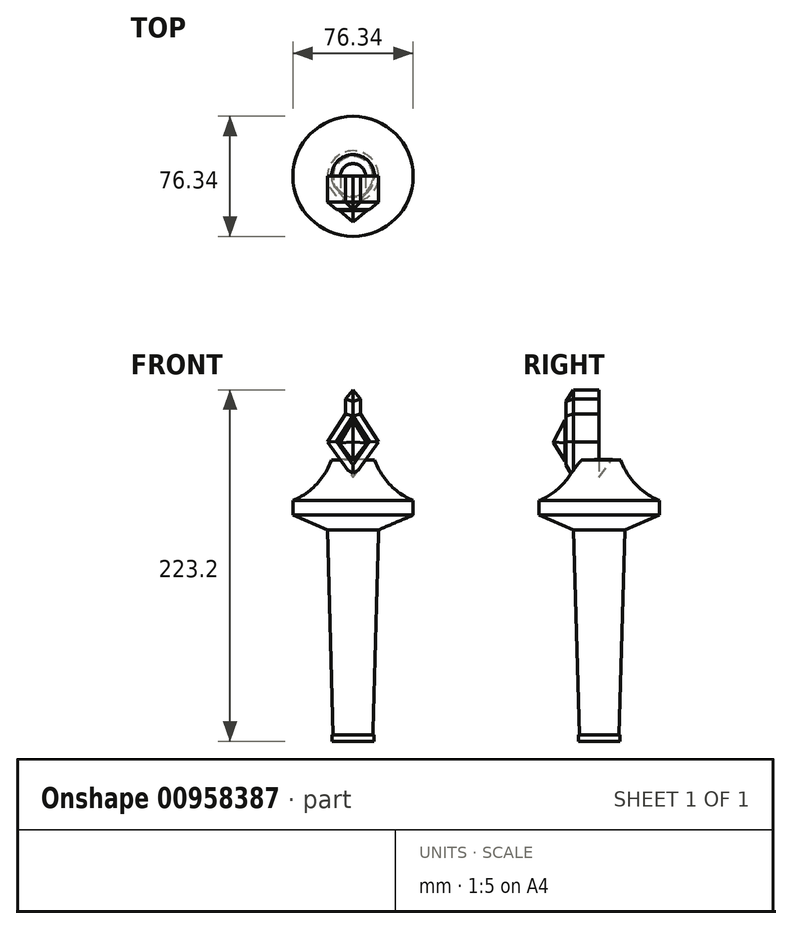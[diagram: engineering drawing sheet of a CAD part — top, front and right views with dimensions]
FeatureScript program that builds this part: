
annotation { "Feature Type Name" : "Feature", "Feature Type Description" : "" }
export const myFeature = defineFeature(function(context is Context, id is Id, definition is map)
    precondition{}
    {
        {
            var Q0;
            Q0=qCreatedBy(makeId("Front.planeOp"),FACE);
            var sketch = newSketch(context, id + "F0", { "sketchPlane" : qUnion([Q0])});
            skPoint(sketch, "E0", {"position": v(0, 703.66) * mm});
            skPoint(sketch, "E1", {"position": v(-33.04, 561.22) * mm});
            skPoint(sketch, "E2", {"position": v(33.12, 559.68) * mm});
            skPoint(sketch, "E3", {"position": v(0, 643.14) * mm});
            skPoint(sketch, "E4", {"position": v(-21.24, 561.22) * mm});
            skPoint(sketch, "E5", {"position": v(21.32, 559.68) * mm});
            skArc(sketch, "E6", {"start": v(0, 703.66) * mm, "mid": v(-24.36, 634.26) * mm, "end": v(-33.04, 561.22) * mm});
            skArc(sketch, "E7", {"start": v(0, 643.14) * mm, "mid": v(-14.32, 603.14) * mm, "end": v(-21.24, 561.22) * mm});
            skLineSegment(sketch, "E8", {"start": v(-21.24, 561.22) * mm, "end": v(-21.24, 29.21) * mm});
            skLineSegment(sketch, "E9", {"start": v(-33.04, 561.22) * mm, "end": v(-33.04, 29.21) * mm});
            skArc(sketch, "E10", {"start": v(-40.37, 9.8) * mm, "mid": v(-34.93, 18.84) * mm, "end": v(-33.04, 29.21) * mm});
            skLineSegment(sketch, "E11", {"start": v(-40.37, 9.8) * mm, "end": v(-40.37, -9.8) * mm});
            skArc(sketch, "E12", {"start": v(-40.37, 6.38) * mm, "mid": v(-27.78, 15.27) * mm, "end": v(-21.24, 29.21) * mm});
            skArc(sketch, "E13", {"start": v(-22.49, -47.92) * mm, "mid": v(-27.18, -26.87) * mm, "end": v(-40.37, -9.8) * mm});
            skArc(sketch, "E14", {"start": v(-17.65, -33.47) * mm, "mid": v(-24.1, -16.05) * mm, "end": v(-40.37, -7.05) * mm});
            skArc(sketch, "E15", {"start": v(-13.67, -33.68) * mm, "mid": v(-21.5, -14.83) * mm, "end": v(-40.37, -7.05) * mm});
            skLineSegment(sketch, "E16", {"start": v(-22.49, -47.92) * mm, "end": v(-22.49, -67.64) * mm});
            skLineSegment(sketch, "E17", {"start": v(-17.65, -33.47) * mm, "end": v(-17.65, -67.15) * mm});
            skLineSegment(sketch, "E18", {"start": v(-13.67, -33.68) * mm, "end": v(-13.67, -69.09) * mm});
            skArc(sketch, "E19", {"start": v(-24.53, -68.9) * mm, "mid": v(-20.97, -68.48) * mm, "end": v(-17.65, -67.15) * mm});
            skArc(sketch, "E20", {"start": v(-24.53, -68.9) * mm, "mid": v(-25.56, -70.66) * mm, "end": v(-24.53, -72.41) * mm});
            skArc(sketch, "E21", {"start": v(-24.53, -72.41) * mm, "mid": v(-18.82, -71.64) * mm, "end": v(-13.67, -69.09) * mm});
            skArc(sketch, "E22", {"start": v(-24.53, -72.41) * mm, "mid": v(-25.73, -74.3) * mm, "end": v(-24.53, -76.18) * mm});
            skArc(sketch, "E23", {"start": v(-24.53, -76.18) * mm, "mid": v(-18.95, -75.47) * mm, "end": v(-13.67, -73.57) * mm});
            skArc(sketch, "E24", {"start": v(-24.53, -76.18) * mm, "mid": v(-25.79, -78.54) * mm, "end": v(-24.53, -80.9) * mm});
            skArc(sketch, "E25", {"start": v(-24.53, -80.9) * mm, "mid": v(-18.9, -79.64) * mm, "end": v(-13.67, -77.23) * mm});
            skArc(sketch, "E26", {"start": v(-13.67, -73.57) * mm, "mid": v(-12.6, -71.33) * mm, "end": v(-13.67, -69.09) * mm});
            skArc(sketch, "E27", {"start": v(-13.67, -77.23) * mm, "mid": v(-12.78, -75.4) * mm, "end": v(-13.67, -73.57) * mm});
            skLineSegment(sketch, "E28", {"start": v(-22.49, -67.64) * mm, "end": v(-22.49, -68.78) * mm});
            skLineSegment(sketch, "E29", {"start": v(-13.67, -77.23) * mm, "end": v(-13.67, -82.87) * mm});
            skLineSegment(sketch, "E30", {"start": v(-13.67, -82.87) * mm, "end": v(-4.24, -95.34) * mm});
            skLineSegment(sketch, "E31", {"start": v(-4.24, -95.34) * mm, "end": v(-0.17, -90.29) * mm});
            skLineSegment(sketch, "E32", {"start": v(-4.24, -95.34) * mm, "end": v(-4.7, -95.91) * mm});
            skLineSegment(sketch, "E33", {"start": v(-4.7, -95.91) * mm, "end": v(-4.7, -105.38) * mm});
            skLineSegment(sketch, "E34", {"start": v(-4.7, -105.38) * mm, "end": v(-16.08, -123.1) * mm});
            skLineSegment(sketch, "E35", {"start": v(-16.08, -123.1) * mm, "end": v(0, -145.74) * mm});
            skLineSegment(sketch, "E36", {"start": v(0, -135.29) * mm, "end": v(-8.73, -123.74) * mm});
            skLineSegment(sketch, "E37", {"start": v(-8.73, -123.74) * mm, "end": v(-0.34, -109.73) * mm});
            skLineSegment(sketch, "E38", {"start": v(-24.1, -80.84) * mm, "end": v(-24.53, -107.1) * mm});
            skArc(sketch, "E39", {"start": v(-27.48, -112) * mm, "mid": v(-25.34, -109.95) * mm, "end": v(-24.53, -107.1) * mm});
            skLineSegment(sketch, "E40", {"start": v(-27.75, -112) * mm, "end": v(-29.68, -110.54) * mm});
            skArc(sketch, "E41", {"start": v(-27.75, -112) * mm, "mid": v(-27.61, -112.05) * mm, "end": v(-27.48, -112) * mm});
            skLineSegment(sketch, "E42", {"start": v(-63.06, -110.54) * mm, "end": v(-115.4, -93.1) * mm});
            skArc(sketch, "E43", {"start": v(-115.4, -93.1) * mm, "mid": v(-100.03, -130.8) * mm, "end": v(-72.52, -160.81) * mm});
            skArc(sketch, "E44", {"start": v(-38.17, -160.39) * mm, "mid": v(-23.44, -150.33) * mm, "end": v(-13.92, -135.25) * mm});
            skLineSegment(sketch, "E45", {"start": v(-72.52, -160.81) * mm, "end": v(-71.25, -178.99) * mm});
            skArc(sketch, "E46", {"start": v(-21.13, -147.73) * mm, "mid": v(-49.45, -158.13) * mm, "end": v(-71.25, -178.99) * mm});
            skLineSegment(sketch, "E47", {"start": v(-38.17, -160.39) * mm, "end": v(-38.17, -169.66) * mm});
            skLineSegment(sketch, "E48", {"start": v(-38.17, -169.66) * mm, "end": v(-16.2, -178.99) * mm});
            skArc(sketch, "E49", {"start": v(-8.04, -134.42) * mm, "mid": v(-46.52, -146.96) * mm, "end": v(-71.25, -178.99) * mm});
            skLineSegment(sketch, "E50", {"start": v(-13.92, -135.25) * mm, "end": v(-13.74, -134.75) * mm});
            skLineSegment(sketch, "E51", {"start": v(-38.17, -160.39) * mm, "end": v(0, -160.39) * mm});
            skLineSegment(sketch, "E52", {"start": v(-38.17, -169.66) * mm, "end": v(0, -169.66) * mm});
            skLineSegment(sketch, "E53", {"start": v(-16.2, -178.99) * mm, "end": v(0, -178.99) * mm});
            skLineSegment(sketch, "E54", {"start": v(-16.2, -178.99) * mm, "end": v(-12.57, -309.2) * mm});
            skLineSegment(sketch, "E55", {"start": v(-12.57, -309.2) * mm, "end": v(0, -309.2) * mm});
            skLineSegment(sketch, "E56", {"start": v(-12.57, -309.2) * mm, "end": v(-13.23, -309.23) * mm});
            skArc(sketch, "E57", {"start": v(-25.71, -322.33) * mm, "mid": v(-20.12, -318.1) * mm, "end": v(-15.03, -313.28) * mm});
            skArc(sketch, "E58", {"start": v(-25.71, -322.33) * mm, "mid": v(-22.52, -329.43) * mm, "end": v(-16.45, -334.3) * mm});
            skLineSegment(sketch, "E59", {"start": v(-25.71, -322.33) * mm, "end": v(0, -322.33) * mm});
            skLineSegment(sketch, "E60", {"start": v(-16.45, -334.3) * mm, "end": v(-13.88, -331.84) * mm});
            skLineSegment(sketch, "E61", {"start": v(-13.88, -331.84) * mm, "end": v(-6.83, -336.27) * mm});
            skLineSegment(sketch, "E62", {"start": v(-6.83, -336.27) * mm, "end": v(0, -329.87) * mm});
            skLineSegment(sketch, "E63", {"start": v(-16.45, -334.3) * mm, "end": v(-9.32, -357.85) * mm});
            skLineSegment(sketch, "E64", {"start": v(-9.32, -357.85) * mm, "end": v(0, -357.85) * mm});
            skLineSegment(sketch, "E65", {"start": v(-6.83, -336.27) * mm, "end": v(-3.99, -357.85) * mm});
            skLineSegment(sketch, "E66", {"start": v(-15.03, -313.28) * mm, "end": v(0, -313.28) * mm});
            skLineSegment(sketch, "E67", {"start": v(-13.23, -309.23) * mm, "end": v(-13.23, -313.28) * mm});
            skArc(sketch, "E68.MirrorCS", {"start": v(13.67, -77.23) * mm, "mid": v(12.78, -75.4) * mm, "end": v(13.67, -73.57) * mm});
            skArc(sketch, "E69.MirrorCS", {"start": v(24.53, -68.9) * mm, "mid": v(20.97, -68.48) * mm, "end": v(17.65, -67.15) * mm});
            skArc(sketch, "E70.MirrorCS", {"start": v(24.53, -76.18) * mm, "mid": v(18.95, -75.47) * mm, "end": v(13.67, -73.57) * mm});
            skArc(sketch, "E71.MirrorCS", {"start": v(24.53, -72.41) * mm, "mid": v(18.82, -71.64) * mm, "end": v(13.67, -69.09) * mm});
            skArc(sketch, "E72.MirrorCS", {"start": v(24.53, -68.9) * mm, "mid": v(25.56, -70.66) * mm, "end": v(24.53, -72.41) * mm});
            skArc(sketch, "E73.MirrorCS", {"start": v(24.53, -76.18) * mm, "mid": v(25.79, -78.54) * mm, "end": v(24.53, -80.9) * mm});
            skLineSegment(sketch, "E74.MirrorCS", {"start": v(13.67, -77.23) * mm, "end": v(13.67, -82.87) * mm});
            skArc(sketch, "E75.MirrorCS", {"start": v(24.53, -72.41) * mm, "mid": v(25.73, -74.3) * mm, "end": v(24.53, -76.18) * mm});
            skArc(sketch, "E76.MirrorCS", {"start": v(24.53, -80.9) * mm, "mid": v(18.9, -79.64) * mm, "end": v(13.67, -77.23) * mm});
            skLineSegment(sketch, "E77.MirrorCS", {"start": v(22.49, -47.92) * mm, "end": v(22.49, -67.64) * mm});
            skArc(sketch, "E78.MirrorCS", {"start": v(13.67, -73.57) * mm, "mid": v(12.6, -71.33) * mm, "end": v(13.67, -69.09) * mm});
            skLineSegment(sketch, "E79.MirrorCS", {"start": v(24.1, -80.84) * mm, "end": v(24.53, -107.1) * mm});
            skLineSegment(sketch, "E80.MirrorCS", {"start": v(13.88, -331.84) * mm, "end": v(6.83, -336.27) * mm});
            skLineSegment(sketch, "E81.MirrorCS", {"start": v(12.57, -309.2) * mm, "end": v(13.23, -309.23) * mm});
            skLineSegment(sketch, "E82.MirrorCS", {"start": v(27.75, -112) * mm, "end": v(29.68, -110.54) * mm});
            skLineSegment(sketch, "E83.MirrorCS", {"start": v(16.45, -334.3) * mm, "end": v(13.88, -331.84) * mm});
            skArc(sketch, "E84.MirrorCS", {"start": v(27.75, -112) * mm, "mid": v(27.61, -112.05) * mm, "end": v(27.48, -112) * mm});
            skArc(sketch, "E85.MirrorCS", {"start": v(27.48, -112) * mm, "mid": v(25.34, -109.95) * mm, "end": v(24.53, -107.1) * mm});
            skLineSegment(sketch, "E86.MirrorCS", {"start": v(13.23, -309.23) * mm, "end": v(13.23, -313.28) * mm});
            skArc(sketch, "E87.MirrorCS", {"start": v(25.71, -322.33) * mm, "mid": v(20.12, -318.1) * mm, "end": v(15.03, -313.28) * mm});
            skArc(sketch, "E88.MirrorCS", {"start": v(25.71, -322.33) * mm, "mid": v(22.52, -329.43) * mm, "end": v(16.45, -334.3) * mm});
            skLineSegment(sketch, "E89.MirrorCS", {"start": v(13.92, -135.25) * mm, "end": v(13.74, -134.75) * mm});
            skLineSegment(sketch, "E90.MirrorCS", {"start": v(13.67, -33.68) * mm, "end": v(13.67, -69.09) * mm});
            skArc(sketch, "E91.MirrorCS", {"start": v(38.17, -160.39) * mm, "mid": v(23.44, -150.33) * mm, "end": v(13.92, -135.25) * mm});
            skLineSegment(sketch, "E92.MirrorCS", {"start": v(17.65, -33.47) * mm, "end": v(17.65, -67.15) * mm});
            skLineSegment(sketch, "E93.MirrorCS", {"start": v(38.17, -160.39) * mm, "end": v(38.17, -169.66) * mm});
            skArc(sketch, "E94.MirrorCS", {"start": v(22.49, -47.92) * mm, "mid": v(27.18, -26.87) * mm, "end": v(40.37, -9.8) * mm});
            skLineSegment(sketch, "E95.MirrorCS", {"start": v(40.37, 9.8) * mm, "end": v(40.37, -9.8) * mm});
            skArc(sketch, "E96.MirrorCS", {"start": v(21.13, -147.73) * mm, "mid": v(49.45, -158.13) * mm, "end": v(71.25, -178.99) * mm});
            skArc(sketch, "E97.MirrorCS", {"start": v(17.65, -33.47) * mm, "mid": v(24.1, -16.05) * mm, "end": v(40.37, -7.05) * mm});
            skArc(sketch, "E98.MirrorCS", {"start": v(40.37, 6.38) * mm, "mid": v(27.78, 15.27) * mm, "end": v(21.24, 29.21) * mm});
            skLineSegment(sketch, "E99.MirrorCS", {"start": v(38.17, -169.66) * mm, "end": v(16.2, -178.99) * mm});
            skArc(sketch, "E100.MirrorCS", {"start": v(40.37, 9.8) * mm, "mid": v(34.93, 18.84) * mm, "end": v(33.04, 29.21) * mm});
            skLineSegment(sketch, "E101.MirrorCS", {"start": v(72.52, -160.81) * mm, "end": v(71.25, -178.99) * mm});
            skArc(sketch, "E102.MirrorCS", {"start": v(29.68, -110.54) * mm, "mid": v(42.8, -118.03) * mm, "end": v(53.66, -128.53) * mm});
            skLineSegment(sketch, "E103.MirrorCS", {"start": v(16.45, -334.3) * mm, "end": v(9.32, -357.85) * mm});
            skArc(sketch, "E104.MirrorCS", {"start": v(13.67, -33.68) * mm, "mid": v(21.5, -14.83) * mm, "end": v(40.37, -7.05) * mm});
            skArc(sketch, "E105.MirrorCS", {"start": v(8.04, -134.42) * mm, "mid": v(46.52, -146.96) * mm, "end": v(71.25, -178.99) * mm});
            skLineSegment(sketch, "E106.MirrorCS", {"start": v(63.06, -110.54) * mm, "end": v(115.4, -93.1) * mm});
            skPoint(sketch, "E107.MirrorP", {"position": v(-21.32, 559.68) * mm});
            skPoint(sketch, "E108.MirrorP", {"position": v(21.24, 561.22) * mm});
            skArc(sketch, "E109.MirrorCS", {"start": v(115.4, -93.1) * mm, "mid": v(100.03, -130.8) * mm, "end": v(72.52, -160.81) * mm});
            skLineSegment(sketch, "E110.MirrorCS", {"start": v(16.2, -178.99) * mm, "end": v(12.57, -309.2) * mm});
            skPoint(sketch, "E111.MirrorP", {"position": v(33.04, 561.22) * mm});
            skLineSegment(sketch, "E112.MirrorCS", {"start": v(21.24, 561.22) * mm, "end": v(21.24, 29.21) * mm});
            skLineSegment(sketch, "E113.MirrorCS", {"start": v(33.04, 561.22) * mm, "end": v(33.04, 29.21) * mm});
            skLineSegment(sketch, "E114.MirrorCS", {"start": v(4.7, -105.38) * mm, "end": v(16.08, -123.1) * mm});
            skLineSegment(sketch, "E115.MirrorCS", {"start": v(8.73, -123.74) * mm, "end": v(0.34, -109.73) * mm});
            skLineSegment(sketch, "E116.MirrorCS", {"start": v(4.7, -95.91) * mm, "end": v(4.7, -105.38) * mm});
            skLineSegment(sketch, "E117.MirrorCS", {"start": v(4.24, -95.34) * mm, "end": v(0.17, -90.29) * mm});
            skLineSegment(sketch, "E118.MirrorCS", {"start": v(4.24, -95.34) * mm, "end": v(4.7, -95.91) * mm});
            skLineSegment(sketch, "E119.MirrorCS", {"start": v(16.08, -123.1) * mm, "end": v(0, -145.74) * mm});
            skLineSegment(sketch, "E120.MirrorCS", {"start": v(0, -135.29) * mm, "end": v(8.73, -123.74) * mm});
            skLineSegment(sketch, "E121.MirrorCS", {"start": v(13.67, -82.87) * mm, "end": v(4.24, -95.34) * mm});
            skLineSegment(sketch, "E122.MirrorCS", {"start": v(38.17, -160.39) * mm, "end": v(0, -160.39) * mm});
            skLineSegment(sketch, "E123.MirrorCS", {"start": v(38.17, -169.66) * mm, "end": v(0, -169.66) * mm});
            skLineSegment(sketch, "E124.MirrorCS", {"start": v(16.2, -178.99) * mm, "end": v(0, -178.99) * mm});
            skLineSegment(sketch, "E125.MirrorCS", {"start": v(12.57, -309.2) * mm, "end": v(0, -309.2) * mm});
            skLineSegment(sketch, "E126.MirrorCS", {"start": v(15.03, -313.28) * mm, "end": v(0, -313.28) * mm});
            skLineSegment(sketch, "E127.MirrorCS", {"start": v(25.71, -322.33) * mm, "end": v(0, -322.33) * mm});
            skLineSegment(sketch, "E128.MirrorCS", {"start": v(6.83, -336.27) * mm, "end": v(0, -329.87) * mm});
            skLineSegment(sketch, "E129.MirrorCS", {"start": v(6.83, -336.27) * mm, "end": v(3.99, -357.85) * mm});
            skLineSegment(sketch, "E130.MirrorCS", {"start": v(9.32, -357.85) * mm, "end": v(0, -357.85) * mm});
            skArc(sketch, "E131.MirrorCS", {"start": v(0, 643.14) * mm, "mid": v(14.32, 603.14) * mm, "end": v(21.24, 561.22) * mm});
            skArc(sketch, "E132.MirrorCS", {"start": v(0, 703.66) * mm, "mid": v(24.36, 634.26) * mm, "end": v(33.04, 561.22) * mm});
            skLineSegment(sketch, "E133", {"start": v(-0.17, -90.29) * mm, "end": v(0, -90.08) * mm});
            skLineSegment(sketch, "E134", {"start": v(0, -90.08) * mm, "end": v(0.17, -90.29) * mm});
            skLineSegment(sketch, "E135", {"start": v(-0.34, -109.73) * mm, "end": v(0, -109.16) * mm});
            skLineSegment(sketch, "E136", {"start": v(0, -109.16) * mm, "end": v(0.34, -109.73) * mm});
            skPoint(sketch, "E137", {"position": v(0, 164.41) * mm});
            skArc(sketch, "E138", {"start": v(-80.57, -104.7) * mm, "mid": v(-69.3, -129.83) * mm, "end": v(-52, -151.26) * mm});
            skArc(sketch, "E139", {"start": v(-63.06, -110.54) * mm, "mid": v(-54.81, -128.77) * mm, "end": v(-41.58, -143.79) * mm});
            skArc(sketch, "E140", {"start": v(-29.68, -110.54) * mm, "mid": v(-43.29, -118.25) * mm, "end": v(-54.72, -128.92) * mm});
            skArc(sketch, "E141", {"start": v(-98.3, -98.8) * mm, "mid": v(-82.96, -131.43) * mm, "end": v(-59.25, -158.6) * mm});
            skArc(sketch, "E142", {"start": v(-16.08, -123.1) * mm, "mid": v(-21.6, -117.23) * mm, "end": v(-27.75, -112) * mm});
            skArc(sketch, "E143", {"start": v(-17.13, -121.89) * mm, "mid": v(-33.8, -127.29) * mm, "end": v(-47.85, -137.78) * mm});
            skArc(sketch, "E144", {"start": v(-12.17, -128.6) * mm, "mid": v(-30.11, -130.96) * mm, "end": v(-45.87, -139.85) * mm});
            skArc(sketch, "E145", {"start": v(-14.16, -91.7) * mm, "mid": v(-19.14, -95.73) * mm, "end": v(-16.74, -101.66) * mm});
            skArc(sketch, "E146", {"start": v(-8.1, -101.66) * mm, "mid": v(-8.9, -95.32) * mm, "end": v(-14.16, -91.7) * mm});
            skArc(sketch, "E147", {"start": v(-20.32, -118.49) * mm, "mid": v(-12.8, -111.1) * mm, "end": v(-8.1, -101.66) * mm});
            skArc(sketch, "E148", {"start": v(-23.06, -115.9) * mm, "mid": v(-15.04, -109.05) * mm, "end": v(-11.6, -99.09) * mm});
            skArc(sketch, "E149", {"start": v(-16.74, -96.05) * mm, "mid": v(-17.17, -98.85) * mm, "end": v(-16.74, -101.66) * mm});
            skArc(sketch, "E150", {"start": v(-12.37, -95.38) * mm, "mid": v(-14.76, -94.34) * mm, "end": v(-16.74, -96.05) * mm});
            skArc(sketch, "E151", {"start": v(-11.6, -99.09) * mm, "mid": v(-11.6, -97.16) * mm, "end": v(-12.37, -95.38) * mm});
            skArc(sketch, "E152.MirrorCS", {"start": v(23.06, -115.9) * mm, "mid": v(15.04, -109.05) * mm, "end": v(11.6, -99.09) * mm});
            skArc(sketch, "E153.MirrorCS", {"start": v(20.32, -118.49) * mm, "mid": v(12.8, -111.1) * mm, "end": v(8.1, -101.66) * mm});
            skArc(sketch, "E154.MirrorCS", {"start": v(8.1, -101.66) * mm, "mid": v(8.9, -95.32) * mm, "end": v(14.16, -91.7) * mm});
            skArc(sketch, "E155.MirrorCS", {"start": v(14.16, -91.7) * mm, "mid": v(19.14, -95.73) * mm, "end": v(16.74, -101.66) * mm});
            skArc(sketch, "E156.MirrorCS", {"start": v(12.37, -95.38) * mm, "mid": v(14.76, -94.34) * mm, "end": v(16.74, -96.05) * mm});
            skArc(sketch, "E157.MirrorCS", {"start": v(11.6, -99.09) * mm, "mid": v(11.6, -97.16) * mm, "end": v(12.37, -95.38) * mm});
            skArc(sketch, "E158.MirrorCS", {"start": v(16.74, -96.05) * mm, "mid": v(17.17, -98.85) * mm, "end": v(16.74, -101.66) * mm});
            skArc(sketch, "E159.MirrorCS", {"start": v(16.08, -123.1) * mm, "mid": v(21.6, -117.23) * mm, "end": v(27.75, -112) * mm});
            skArc(sketch, "E160.MirrorCS", {"start": v(17.13, -121.89) * mm, "mid": v(33.8, -127.29) * mm, "end": v(47.85, -137.78) * mm});
            skArc(sketch, "E161.MirrorCS", {"start": v(12.17, -128.6) * mm, "mid": v(30.11, -130.96) * mm, "end": v(45.87, -139.85) * mm});
            skArc(sketch, "E162.MirrorCS", {"start": v(63.06, -110.54) * mm, "mid": v(54.81, -128.77) * mm, "end": v(41.58, -143.79) * mm});
            skArc(sketch, "E163.MirrorCS", {"start": v(80.57, -104.7) * mm, "mid": v(69.3, -129.83) * mm, "end": v(52, -151.26) * mm});
            skArc(sketch, "E164.MirrorCS", {"start": v(98.3, -98.8) * mm, "mid": v(82.96, -131.43) * mm, "end": v(59.25, -158.6) * mm});
            skLineSegment(sketch, "E165", {"start": v(0, -145.74) * mm, "end": v(0, -357.85) * mm});
            skPoint(sketch, "E166", {"position": v(40.37, 0) * mm});
            skLineSegment(sketch, "E167", {"start": v(40.37, 0) * mm, "end": v(-40.37, 0) * mm, "construction": true});
            skLineSegment(sketch, "E168", {"start": v(22.49, -67.64) * mm, "end": v(22.49, -68.78) * mm});
            skPoint(sketch, "E169", {"position": v(0, 0) * mm});
            skArc(sketch, "E170", {"start": v(54.38, -129.43) * mm, "mid": v(54.02, -128.98) * mm, "end": v(53.66, -128.53) * mm});
            skSolve(sketch);
        }
        {
            var Q0;
            {var subQ1=sQuery(id+"F0.wireOp",EDGE,"E89.MirrorCS");Q0=makeQuery(id+"F0.imprint","IMPRINT",FACE,{"disambiguationData":[TD([[makeQuery(id+"F0.imprint","IMPRINT",EDGE,{"derivedFrom":subQ1}),1.0]])]});}
            var Q1;
            Q1=makeQuery(id+"F0.imprint","IMPRINT",FACE,{"disambiguationData":[TD([[makeQuery(id+"F0.imprint","IMPRINT",EDGE,{"derivedFrom":sQuery(id+"F0.wireOp",EDGE,"E93.MirrorCS")}),-1.0]])]});
            var Q2;
            Q2=makeQuery(id+"F0.imprint","IMPRINT",FACE,{"disambiguationData":[TD([[makeQuery(id+"F0.imprint","IMPRINT",EDGE,{"derivedFrom":sQuery(id+"F0.wireOp",EDGE,"E99.MirrorCS")}),-1.0]])]});
            var Q3;
            Q3=makeQuery(id+"F0.imprint","IMPRINT",FACE,{"disambiguationData":[TD([[makeQuery(id+"F0.imprint","IMPRINT",EDGE,{"derivedFrom":sQuery(id+"F0.wireOp",EDGE,"E110.MirrorCS")}),-1.0]])]});
            var Q4;
            Q4=makeQuery(id+"F0.imprint","IMPRINT",FACE,{"disambiguationData":[TD([[makeQuery(id+"F0.imprint","IMPRINT",EDGE,{"derivedFrom":sQuery(id+"F0.wireOp",EDGE,"E81.MirrorCS")}),-1.0]])]});
            var Q5;
            {var subQ5=sQuery(id+"F0.wireOp",EDGE,"E87.MirrorCS");Q5=makeQuery(id+"F0.imprint","IMPRINT",FACE,{"disambiguationData":[TD([[makeQuery(id+"F0.imprint","IMPRINT",EDGE,{"derivedFrom":subQ5}),1.0]])]});}
            var Q6;
            Q6=sQuery(id+"F0.wireOp",EDGE,"E165");
            revolve(context, id + "F1", {"surfaceOperationType" : NewSurfaceOperationType.NEW, "entities" : qUnion([Q0, Q1, Q2, Q3, Q4, Q5]), "axis" : qUnion([Q6]), "revolveType" : RevolveType.FULL});
        }
        {
            var Q0;
            Q0=makeQuery(id+"F0.imprint","IMPRINT",FACE,{"disambiguationData":[TD([[makeQuery(id+"F0.imprint","IMPRINT",EDGE,{"derivedFrom":sQuery(id+"F0.wireOp",EDGE,"E31")}),-1.0]])]});
            extrude(context, id + "F2", {"entities" : qUnion([Q0]), "operationType" : NewBodyOperationType.ADD, "depth" : 21 * mm, "offsetDistance" : 25 * mm});
        }
        {
            var Q0;
            Q0=makeQuery(id+"F0.imprint","IMPRINT",FACE,{"disambiguationData":[TD([[makeQuery(id+"F0.imprint","IMPRINT",EDGE,{"derivedFrom":sQuery(id+"F0.wireOp",EDGE,"E36")}),-1.0]])]});
            extrude(context, id + "F3", {"entities" : qUnion([Q0]), "operationType" : NewBodyOperationType.ADD, "depth" : 29 * mm, "offsetDistance" : 25 * mm});
        }
        {
            var Q0;
            Q0=makeQuery(id+"F3.opExtrude","CAP_FACE",FACE,{"disambiguationData":[OSD([sQuery(id+"F0.wireOp",EDGE,"E36"),sQuery(id+"F0.wireOp",EDGE,"E37"),sQuery(id+"F0.wireOp",EDGE,"E115.MirrorCS"),sQuery(id+"F0.wireOp",EDGE,"E120.MirrorCS"),sQuery(id+"F0.wireOp",EDGE,"E135"),sQuery(id+"F0.wireOp",EDGE,"E136")])],"isStart":false});
            chamfer(context, id + "F4", {"entities" : qUnion([Q0]), "width" : 7.2 * mm, "tangentPropagation" : true});
        }
        {
            var Q0;
            Q0=makeQuery(id+"F2.opExtrude","CAP_EDGE",EDGE,{"disambiguationData":[OSD([sQuery(id+"F0.wireOp",EDGE,"E34")])],"isStart":false});
            var Q1;
            Q1=makeQuery(id+"F2.opExtrude","CAP_EDGE",EDGE,{"disambiguationData":[OSD([sQuery(id+"F0.wireOp",EDGE,"E33")])],"isStart":false});
            var Q2;
            Q2=makeQuery(id+"F2.opExtrude","CAP_EDGE",EDGE,{"disambiguationData":[OSD([sQuery(id+"F0.wireOp",EDGE,"E117.MirrorCS"),sQuery(id+"F0.wireOp",EDGE,"E118.MirrorCS"),sQuery(id+"F0.wireOp",EDGE,"E134")])],"isStart":false});
            var Q3;
            Q3=makeQuery(id+"F2.opExtrude","CAP_EDGE",EDGE,{"disambiguationData":[OSD([sQuery(id+"F0.wireOp",EDGE,"E116.MirrorCS")])],"isStart":false});
            var Q4;
            Q4=makeQuery(id+"F2.opExtrude","CAP_EDGE",EDGE,{"disambiguationData":[OSD([sQuery(id+"F0.wireOp",EDGE,"E114.MirrorCS")])],"isStart":false});
            var Q5;
            Q5=makeQuery(id+"F2.opExtrude","CAP_EDGE",EDGE,{"disambiguationData":[OSD([sQuery(id+"F0.wireOp",EDGE,"E119.MirrorCS")])],"isStart":false});
            var Q6;
            Q6=makeQuery(id+"F2.opExtrude","CAP_EDGE",EDGE,{"disambiguationData":[OSD([sQuery(id+"F0.wireOp",EDGE,"E35")])],"isStart":false});
            var Q7;
            Q7=makeQuery(id+"F2.opExtrude","CAP_EDGE",EDGE,{"disambiguationData":[OSD([sQuery(id+"F0.wireOp",EDGE,"E31"),sQuery(id+"F0.wireOp",EDGE,"E32"),sQuery(id+"F0.wireOp",EDGE,"E133")])],"isStart":false});
            chamfer(context, id + "F5", {"entities" : qUnion([Q0, Q1, Q2, Q3, Q4, Q5, Q6, Q7]), "width" : 4.7 * mm, "tangentPropagation" : true});
        }
    });
